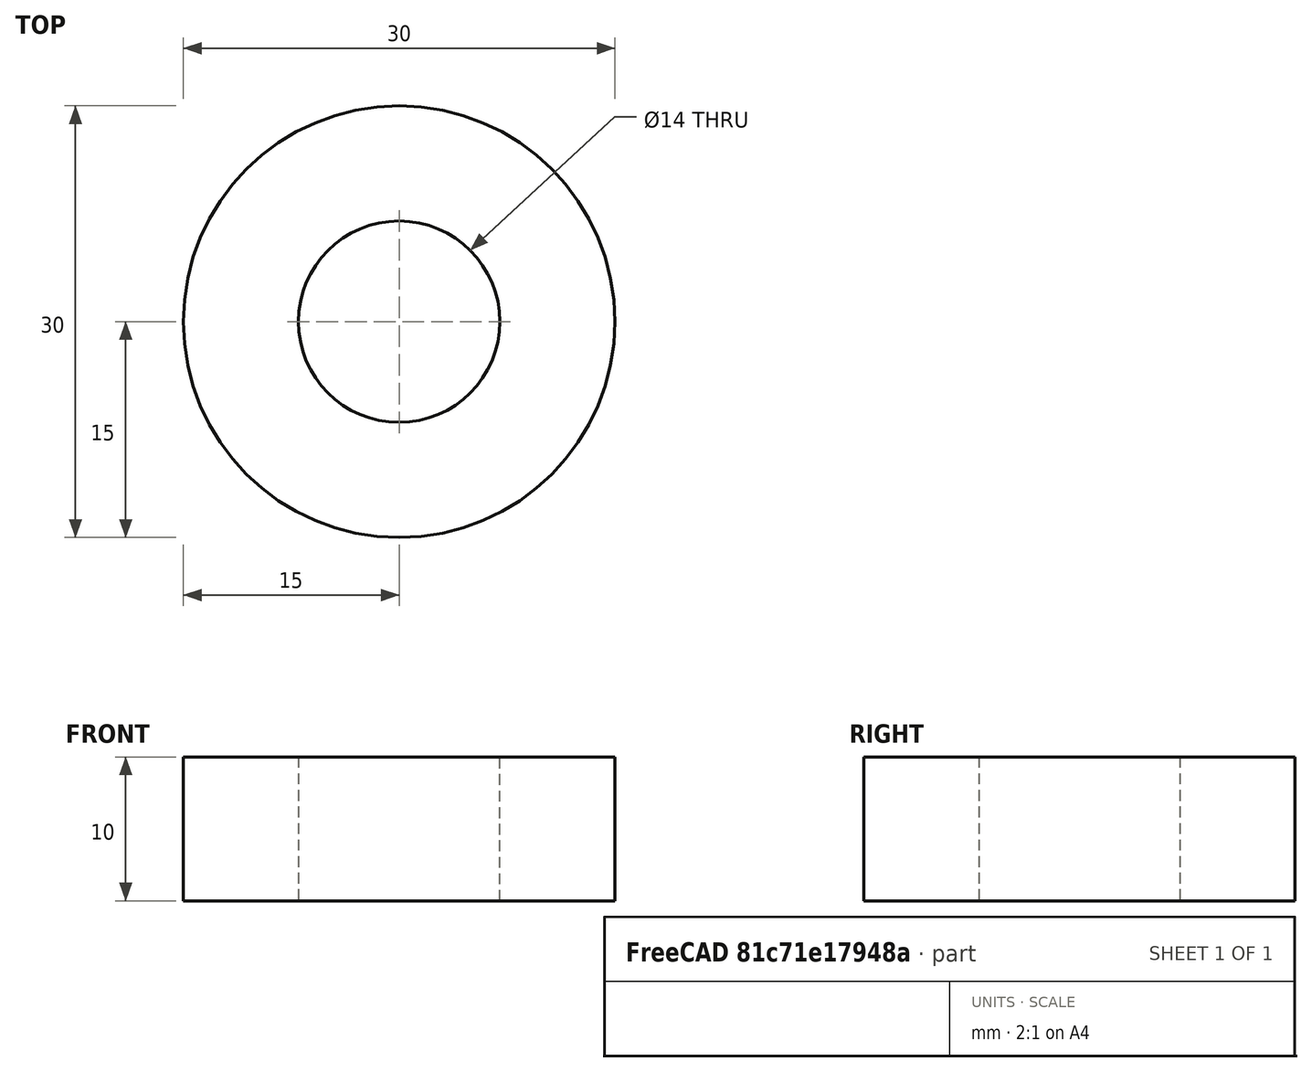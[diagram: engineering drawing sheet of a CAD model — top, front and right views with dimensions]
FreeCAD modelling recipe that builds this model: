
FCSTD DOCUMENT  (FreeCAD 0.20R29177 +426 (Git))
Label: 6201ZZ002_Bearing
License: All rights reserved
LicenseURL: http://en.wikipedia.org/wiki/All_rights_reserved
objects: PartDesign::CoordinateSystem×2, Sketcher::SketchObject×1, PartDesign::Pad×1, PartDesign::Body×1
note: 6 computed .brp shape members not serialized (recipe doc carries the construction recipe); baked Part::Feature solids carry a one-line shape summary decoded from their .brp

FEATURE [Sketcher::SketchObject] Sketch
  FullyConstrained = true
  MapMode = 5
  Support = -> [XY_Plane]
  sketch-geometry (2):
    g0: Circle CenterX=0 CenterY=0 CenterZ=0 NormalX=0 NormalY=0 NormalZ=1 AngleXU=0 Radius=15
    g1: Circle CenterX=0 CenterY=0 CenterZ=0 NormalX=0 NormalY=0 NormalZ=1 AngleXU=0 Radius=7
  constraints (4):
    c: Coincident(g0,g-1)
    c: Diameter(g0) = 30
    c: Coincident(g1,g0)
    c: Diameter(g1) = 14
FEATURE [PartDesign::Pad] Pad
  Direction = (0,0,1)
  Length = 10
  Length2 = 10
  Profile = -> Sketch
  ReferenceAxis = -> Sketch [N_Axis]
  Type = 0
FEATURE [PartDesign::CoordinateSystem] LCS_1
  AttacherType = Attacher::AttachEngine3D
  MapMode = 45
  Placement = pos=(-7.1e-15,-9e-16,10) rot=(0,0,1;0rad)
  Support = -> [Pad]
FEATURE [PartDesign::CoordinateSystem] bottom_LCS
  AttacherType = Attacher::AttachEngine3D
  MapMode = 12
  Placement = pos=(0,0,0) rot=(1,0,0;1.5708rad)
  Support = -> [Pad]
FEATURE [PartDesign::Body] Body  label="Fake_bearing"
  Group = -> [Sketch,Pad,LCS_1,bottom_LCS]
  Origin = -> Origin
  Tip = -> Pad
